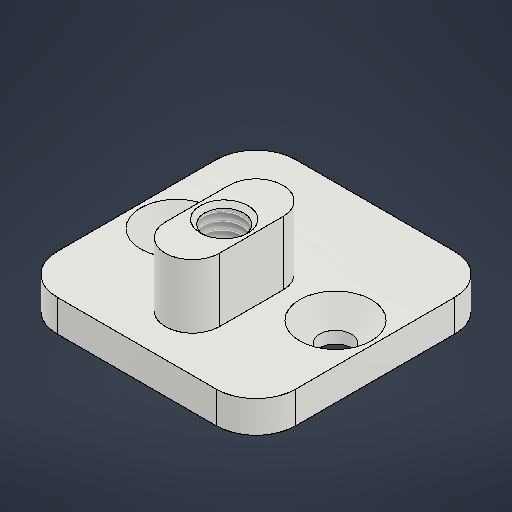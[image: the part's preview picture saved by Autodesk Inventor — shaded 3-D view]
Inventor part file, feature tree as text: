
AUTODESK INVENTOR PART (.ipt)
format: ipt  version: 2025.3 (Build 293356000, 356)  size: 220,672 bytes
history: native  units: mm
features: sketch x2, extrude x2, hole x2, fillet x1
ambient origin geometry x8: Origin, YZ Plane, XZ Plane, XY Plane, X Axis, Y Axis, Z Axis, Center Point
bodies: Solid1 (feature_tree)
feature tree (7):
  sketch  "Sketch1"  dims[d0=30.0mm d1=30.0mm]
  extrude  "Extrusion1"  Depth=30.0mm
  extrude  "Extrusion2"  Depth=8.0mm
  hole  "Hole1"  [1 undecoded]
  hole  "Hole2"  [1 undecoded]
  fillet  "Fillet1"  Radius=12.0mm
  sketch  "Sketch2"  dims[d2=6.8mm d3=8.0mm d4=0.0mm d5=20.0mm d6=12.0mm d7=0.0mm d8=8.0mm d9=0.0mm d10=4.917mm d11=12.0mm d12=6.0mm d13=2.0mm d14=90.0deg d15=8.0mm d16=20.594885mm d17=4.0mm d18=12.0mm d19=9.0mm d20=2.0mm d21=90.0deg d22=8.0mm d23=20.594885mm d24=5.0mm]
note: 2 required parameter values undecoded (feature->parameter linkage not recoverable at this tier; creation-order binding heuristic only, values carry confidence <= 0.55)
